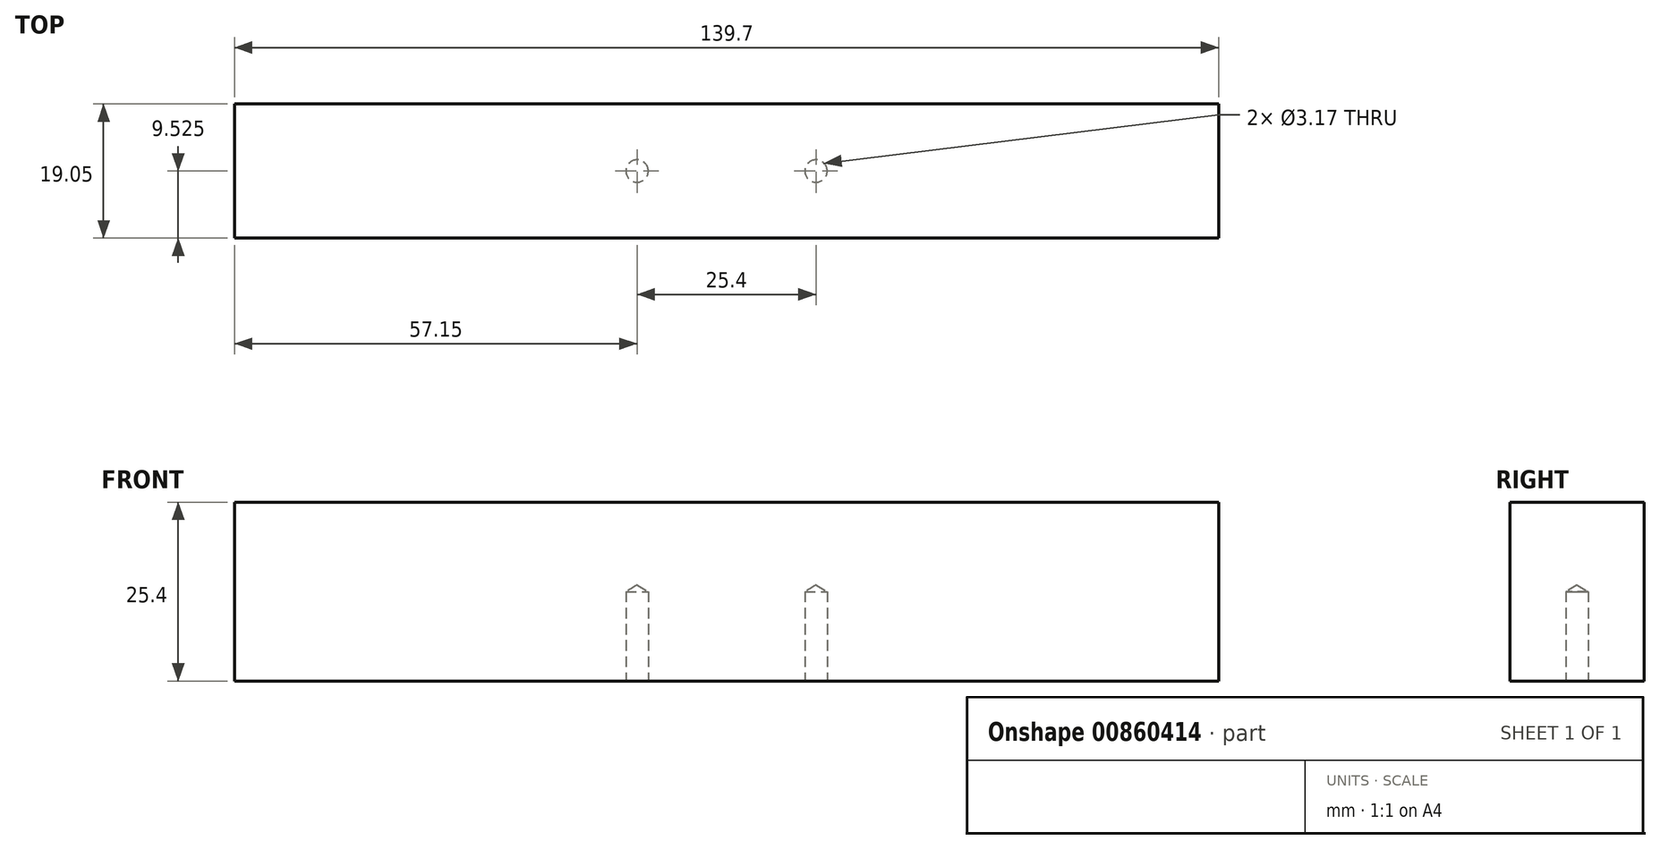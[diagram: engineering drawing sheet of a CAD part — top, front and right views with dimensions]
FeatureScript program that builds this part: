
annotation { "Feature Type Name" : "Feature", "Feature Type Description" : "" }
export const myFeature = defineFeature(function(context is Context, id is Id, definition is map)
    precondition{}
    {
        {
            var Q0;
            Q0=qCreatedBy(makeId("Front.planeOp"),FACE);
            var sketch = newSketch(context, id + "F0", { "sketchPlane" : qUnion([Q0])});
            skLineSegment(sketch, "E0.bottom", {"start": v(-64.52, 41.59) * mm, "end": v(75.18, 41.59) * mm});
            skLineSegment(sketch, "E0.top", {"start": v(-64.52, 16.19) * mm, "end": v(75.18, 16.19) * mm});
            skLineSegment(sketch, "E0.left", {"start": v(-64.52, 41.59) * mm, "end": v(-64.52, 16.19) * mm});
            skLineSegment(sketch, "E0.right", {"start": v(75.18, 41.59) * mm, "end": v(75.18, 16.19) * mm});
            skSolve(sketch);
        }
        {
            var Q0;
            Q0=makeQuery(id+"F0.imprint","IMPRINT",FACE,{"disambiguationData":[TD([[makeQuery(id+"F0.imprint","IMPRINT",EDGE,{"derivedFrom":sQuery(id+"F0.wireOp",EDGE,"E0.bottom")}),-1.0]])]});
            extrude(context, id + "F1", {"entities" : qUnion([Q0]), "depth" : 19.05 * mm, "offsetDistance" : 25.4 * mm});
        }
        {
            var Q0;
            Q0=makeQuery(id+"F1.opExtrude","SWEPT_FACE",FACE,{"disambiguationData":[OSD([sQuery(id+"F0.wireOp",EDGE,"E0.top")])]});
            var sketch = newSketch(context, id + "F2", { "sketchPlane" : qUnion([Q0])});
            skPoint(sketch, "E1", {"position": v(18.03, 9.53) * mm});
            skPoint(sketch, "E2", {"position": v(-7.37, 9.53) * mm});
            skSolve(sketch);
        }
        {
            var Q0;
            Q0=sQuery(id+"F2.wireOp",VERTEX,"E2");
            var Q1;
            Q1=sQuery(id+"F2.wireOp",VERTEX,"E1");
            var Q2;
            Q2=makeQuery(id+"F1.opExtrude","SWEPT_BODY",BODY,{"disambiguationData":[OSD([sQuery(id+"F0.wireOp",EDGE,"E0.bottom"),sQuery(id+"F0.wireOp",EDGE,"E0.top"),sQuery(id+"F0.wireOp",EDGE,"E0.left"),sQuery(id+"F0.wireOp",EDGE,"E0.right")])]});
            hole(context, id + "F3", {"style" : HoleStyle.SIMPLE, "endStyle" : HoleEndStyle.BLIND, "holeDiameter" : 3.17 * mm, "majorDiameter" : 6.35 * mm, "holeDepth" : 12.7 * mm, "isTappedThrough" : true, "tappedDepth" : 12.7 * mm, "tapClearance" : 3, "locations" : qUnion([Q0, Q1]), "scope" : qUnion([Q2])});
        }
    });
